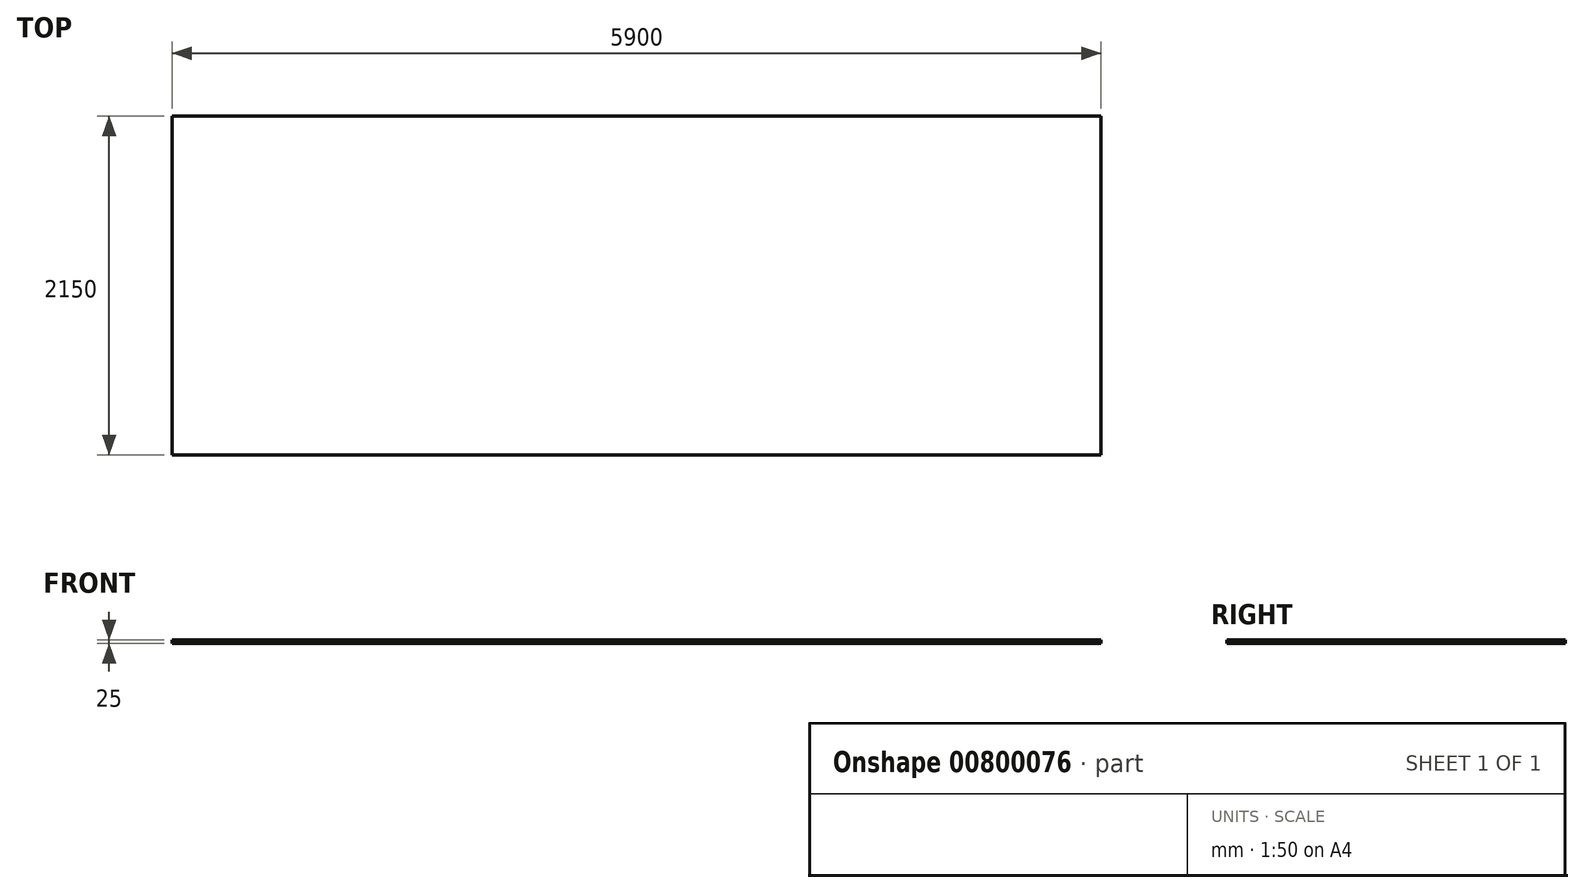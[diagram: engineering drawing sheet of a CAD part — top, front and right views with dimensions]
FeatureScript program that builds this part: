
annotation { "Feature Type Name" : "Feature", "Feature Type Description" : "" }
export const myFeature = defineFeature(function(context is Context, id is Id, definition is map)
    precondition{}
    {
        {
            var Q0;
            Q0=qCreatedBy(makeId("Top.planeOp"),FACE);
            var sketch = newSketch(context, id + "F0", { "sketchPlane" : qUnion([Q0])});
            skLineSegment(sketch, "E0.bottom", {"start": v(2950, -1075) * mm, "end": v(-2950, -1075) * mm});
            skLineSegment(sketch, "E0.top", {"start": v(2950, 1075) * mm, "end": v(-2950, 1075) * mm});
            skLineSegment(sketch, "E0.left", {"start": v(2950, -1075) * mm, "end": v(2950, 1075) * mm});
            skLineSegment(sketch, "E0.right", {"start": v(-2950, -1075) * mm, "end": v(-2950, 1075) * mm});
            skPoint(sketch, "E0.middle", {"position": v(0, 0) * mm});
            skSolve(sketch);
        }
        {
            var Q0;
            Q0=makeQuery(id+"F0.imprint","IMPRINT",FACE,{"disambiguationData":[TD([[makeQuery(id+"F0.imprint","IMPRINT",EDGE,{"derivedFrom":sQuery(id+"F0.wireOp",EDGE,"E0.bottom")}),-1.0]])]});
            extrude(context, id + "F1", {"entities" : qUnion([Q0]), "depth" : 25 * mm, "offsetDistance" : 25 * mm});
        }
    });
